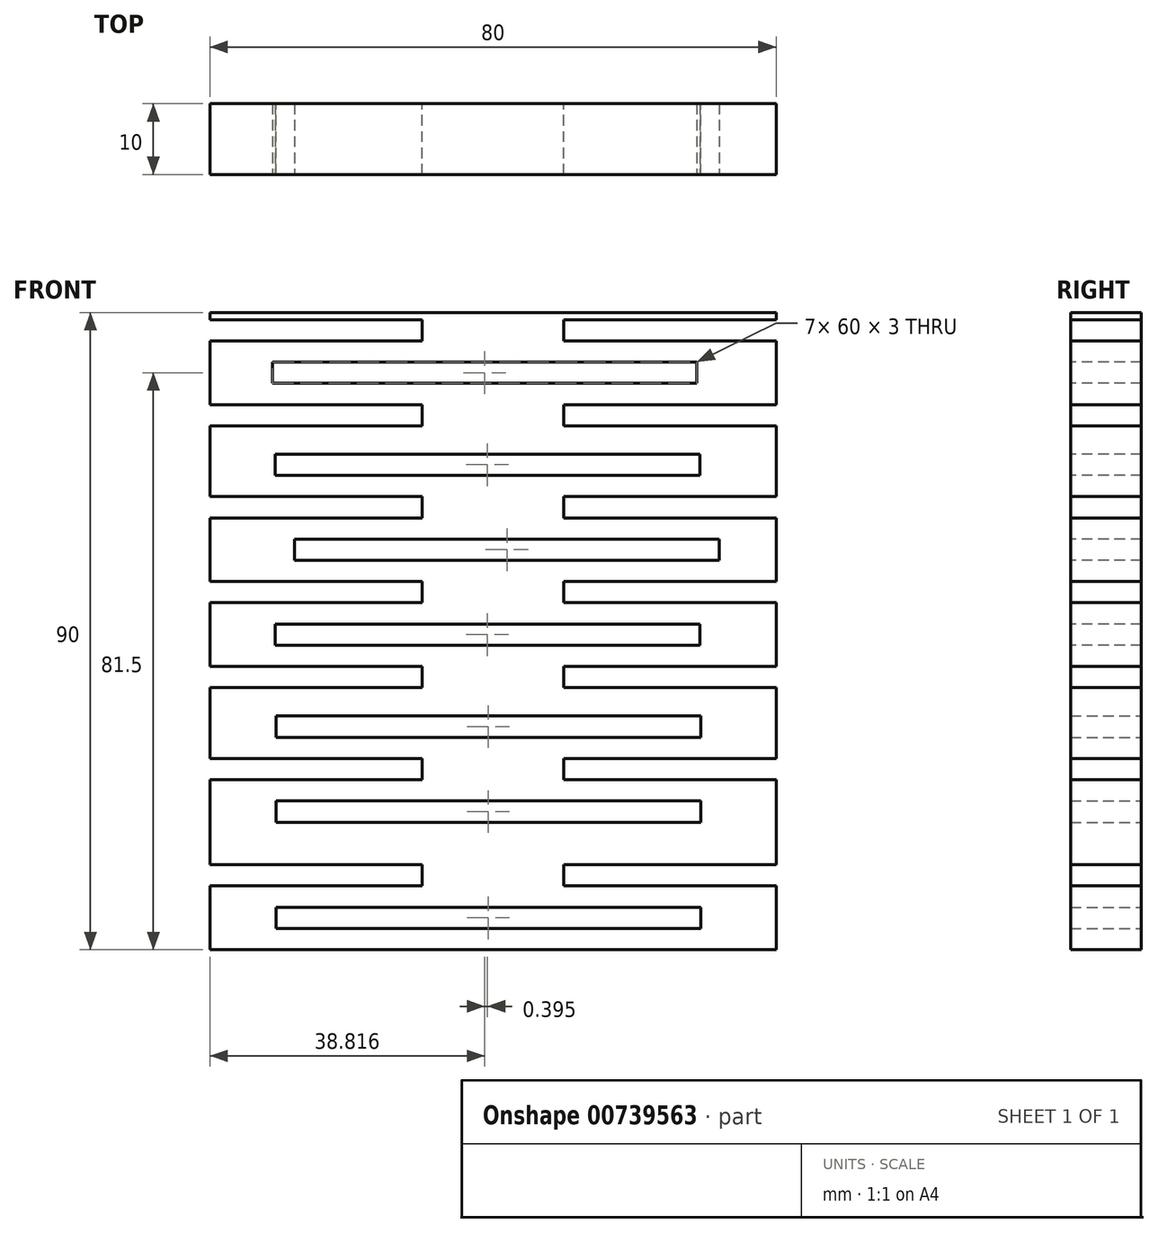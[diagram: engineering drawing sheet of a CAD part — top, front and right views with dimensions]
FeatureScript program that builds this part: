
annotation { "Feature Type Name" : "Feature", "Feature Type Description" : "" }
export const myFeature = defineFeature(function(context is Context, id is Id, definition is map)
    precondition{}
    {
        {
            var Q0;
            Q0=qCreatedBy(makeId("Front.planeOp"),FACE);
            var sketch = newSketch(context, id + "F0", { "sketchPlane" : qUnion([Q0])});
            skPoint(sketch, "E0.firstSnap0", {"position": v(1.21, 52.73) * mm});
            skPoint(sketch, "E0.left.start.orphan", {"position": v(1.21, 53.6) * mm});
            skPoint(sketch, "E1.top.end.orphan", {"position": v(-2.83, 53.6) * mm});
            skPoint(sketch, "E2.left.start.orphan", {"position": v(-45.92, 52.73) * mm});
            skPoint(sketch, "E2.right.start.orphan", {"position": v(48.35, 52.73) * mm});
            skLineSegment(sketch, "E3", {"start": v(40, -40) * mm, "end": v(40, 50) * mm});
            skLineSegment(sketch, "E4", {"start": v(-40, -40) * mm, "end": v(-40, 50) * mm});
            skLineSegment(sketch, "E5", {"start": v(40, 50) * mm, "end": v(-40, 50) * mm});
            skLineSegment(sketch, "E6", {"start": v(40, -40) * mm, "end": v(-40, -40) * mm});
            skPoint(sketch, "E7.start.orphan", {"position": v(-10, -31) * mm});
            skPoint(sketch, "E8.start.orphan", {"position": v(-0.3, -31) * mm});
            skPoint(sketch, "E9.end.orphan", {"position": v(-0.24, -22) * mm});
            skPoint(sketch, "E10.end.orphan", {"position": v(0, -10) * mm});
            skPoint(sketch, "E11.start.orphan", {"position": v(0, -7) * mm});
            skPoint(sketch, "E12.start.orphan", {"position": v(0, 0) * mm});
            skPoint(sketch, "E13.end.orphan", {"position": v(0, 12) * mm});
            skPoint(sketch, "E14.start.orphan", {"position": v(0, 24) * mm});
            skPoint(sketch, "E15.end.orphan", {"position": v(0, 36) * mm});
            skPoint(sketch, "E16.start.orphan", {"position": v(-40, 36) * mm});
            skPoint(sketch, "E17.start.orphan", {"position": v(40, 36) * mm});
            skPoint(sketch, "E18.start.orphan", {"position": v(0, 18) * mm});
            skPoint(sketch, "E19.start.orphan", {"position": v(40, 12) * mm});
            skPoint(sketch, "E20.start.orphan", {"position": v(40, 24) * mm});
            skPoint(sketch, "E21.start.orphan", {"position": v(-40, 24) * mm});
            skPoint(sketch, "E22.start.orphan", {"position": v(-40, 12) * mm});
            skPoint(sketch, "E23.start.orphan", {"position": v(-40, 0) * mm});
            skPoint(sketch, "E24.start.orphan", {"position": v(40, 0) * mm});
            skPoint(sketch, "E25.start.orphan", {"position": v(-0.24, -28) * mm});
            skLineSegment(sketch, "E26", {"start": v(0, 50) * mm, "end": v(0, -40) * mm});
            skLineSegment(sketch, "E27.bottom", {"start": v(-30.66, -37) * mm, "end": v(29.34, -37) * mm});
            skLineSegment(sketch, "E27.top", {"start": v(-30.66, -34) * mm, "end": v(29.34, -34) * mm});
            skLineSegment(sketch, "E27.left", {"start": v(-30.66, -37) * mm, "end": v(-30.66, -34) * mm});
            skLineSegment(sketch, "E27.right", {"start": v(29.34, -37) * mm, "end": v(29.34, -34) * mm});
            skLineSegment(sketch, "E28.bottom", {"start": v(-40, -28) * mm, "end": v(-10, -28) * mm});
            skLineSegment(sketch, "E28.top", {"start": v(-40, -31) * mm, "end": v(-10, -31) * mm});
            skLineSegment(sketch, "E28.left", {"start": v(-40, -28) * mm, "end": v(-40, -31) * mm});
            skLineSegment(sketch, "E28.right", {"start": v(-10, -28) * mm, "end": v(-10, -31) * mm});
            skLineSegment(sketch, "E29.bottom", {"start": v(40, -28) * mm, "end": v(10, -28) * mm});
            skLineSegment(sketch, "E29.top", {"start": v(40, -31) * mm, "end": v(10, -31) * mm});
            skLineSegment(sketch, "E29.left", {"start": v(40, -28) * mm, "end": v(40, -31) * mm});
            skLineSegment(sketch, "E29.right", {"start": v(10, -28) * mm, "end": v(10, -31) * mm});
            skLineSegment(sketch, "E30.bottom", {"start": v(-30.66, -19) * mm, "end": v(29.34, -19) * mm});
            skLineSegment(sketch, "E30.top", {"start": v(-30.66, -22) * mm, "end": v(29.34, -22) * mm});
            skLineSegment(sketch, "E30.left", {"start": v(-30.66, -19) * mm, "end": v(-30.66, -22) * mm});
            skLineSegment(sketch, "E30.right", {"start": v(29.34, -19) * mm, "end": v(29.34, -22) * mm});
            skLineSegment(sketch, "E31.bottom", {"start": v(-40, -13) * mm, "end": v(-10, -13) * mm});
            skLineSegment(sketch, "E31.top", {"start": v(-40, -16) * mm, "end": v(-10, -16) * mm});
            skLineSegment(sketch, "E31.left", {"start": v(-40, -13) * mm, "end": v(-40, -16) * mm});
            skLineSegment(sketch, "E31.right", {"start": v(-10, -13) * mm, "end": v(-10, -16) * mm});
            skLineSegment(sketch, "E32.bottom", {"start": v(10, -13) * mm, "end": v(40, -13) * mm});
            skLineSegment(sketch, "E32.top", {"start": v(10, -16) * mm, "end": v(40, -16) * mm});
            skLineSegment(sketch, "E32.left", {"start": v(10, -13) * mm, "end": v(10, -16) * mm});
            skLineSegment(sketch, "E32.right", {"start": v(40, -13) * mm, "end": v(40, -16) * mm});
            skLineSegment(sketch, "E33.bottom", {"start": v(-20.5, -16) * mm, "end": v(-21.1, -16) * mm});
            skLineSegment(sketch, "E33.top", {"start": v(-20.5, -19) * mm, "end": v(-21.1, -19) * mm});
            skLineSegment(sketch, "E34.bottom", {"start": v(-30.66, -7) * mm, "end": v(29.34, -7) * mm});
            skLineSegment(sketch, "E34.top", {"start": v(-30.66, -10) * mm, "end": v(29.34, -10) * mm});
            skLineSegment(sketch, "E34.left", {"start": v(-30.66, -7) * mm, "end": v(-30.66, -10) * mm});
            skLineSegment(sketch, "E34.right", {"start": v(29.34, -7) * mm, "end": v(29.34, -10) * mm});
            skSolve(sketch);
        }
        {
            var Q0;
            {var subQ9=sQuery(id+"F0.wireOp",EDGE,"E27.left");Q0=makeQuery(id+"F0.imprint","IMPRINT",FACE,{"disambiguationData":[TD([[makeQuery(id+"F0.imprint","IMPRINT",EDGE,{"derivedFrom":subQ9}),1.0]])]});}
            var Q1;
            {var subQ7=sQuery(id+"F0.wireOp",EDGE,"E27.right");Q1=makeQuery(id+"F0.imprint","IMPRINT",FACE,{"disambiguationData":[TD([[makeQuery(id+"F0.imprint","IMPRINT",EDGE,{"derivedFrom":subQ7}),-1.0]])]});}
            extrude(context, id + "F1", {"entities" : qUnion([Q0, Q1]), "depth" : 10 * mm, "offsetDistance" : 25 * mm});
        }
        {
            var Q0;
            Q0=makeQuery(id+"F1.opExtrude","CAP_FACE",FACE,{"disambiguationData":[OSD([sQuery(id+"F0.wireOp",EDGE,"E3"),sQuery(id+"F0.wireOp",EDGE,"E4"),sQuery(id+"F0.wireOp",EDGE,"E5"),sQuery(id+"F0.wireOp",EDGE,"E6"),sQuery(id+"F0.wireOp",EDGE,"E27.bottom"),sQuery(id+"F0.wireOp",EDGE,"E27.top"),sQuery(id+"F0.wireOp",EDGE,"E27.left"),sQuery(id+"F0.wireOp",EDGE,"E27.right"),sQuery(id+"F0.wireOp",EDGE,"E28.bottom"),sQuery(id+"F0.wireOp",EDGE,"E28.top"),sQuery(id+"F0.wireOp",EDGE,"E28.right"),sQuery(id+"F0.wireOp",EDGE,"E29.bottom"),sQuery(id+"F0.wireOp",EDGE,"E29.top"),sQuery(id+"F0.wireOp",EDGE,"E29.right"),sQuery(id+"F0.wireOp",EDGE,"E30.bottom"),sQuery(id+"F0.wireOp",EDGE,"E30.top"),sQuery(id+"F0.wireOp",EDGE,"E30.left"),sQuery(id+"F0.wireOp",EDGE,"E30.right"),sQuery(id+"F0.wireOp",EDGE,"E31.bottom"),sQuery(id+"F0.wireOp",EDGE,"E31.top"),sQuery(id+"F0.wireOp",EDGE,"E31.right"),sQuery(id+"F0.wireOp",EDGE,"E32.bottom"),sQuery(id+"F0.wireOp",EDGE,"E32.top"),sQuery(id+"F0.wireOp",EDGE,"E32.left"),sQuery(id+"F0.wireOp",EDGE,"E33.bottom"),sQuery(id+"F0.wireOp",EDGE,"E33.top"),sQuery(id+"F0.wireOp",EDGE,"E34.bottom"),sQuery(id+"F0.wireOp",EDGE,"E34.top"),sQuery(id+"F0.wireOp",EDGE,"E34.left"),sQuery(id+"F0.wireOp",EDGE,"E34.right")])],"isStart":false});
            var sketch = newSketch(context, id + "F2", { "sketchPlane" : qUnion([Q0])});
            skLineSegment(sketch, "E35.bottom", {"start": v(-40, 0) * mm, "end": v(-10, 0) * mm});
            skLineSegment(sketch, "E35.top", {"start": v(-40, -3) * mm, "end": v(-10, -3) * mm});
            skLineSegment(sketch, "E35.left", {"start": v(-40, 0) * mm, "end": v(-40, -3) * mm});
            skLineSegment(sketch, "E35.right", {"start": v(-10, 0) * mm, "end": v(-10, -3) * mm});
            skLineSegment(sketch, "E36.bottom", {"start": v(40, 0) * mm, "end": v(10, 0) * mm});
            skLineSegment(sketch, "E36.top", {"start": v(40, -3) * mm, "end": v(10, -3) * mm});
            skLineSegment(sketch, "E36.left", {"start": v(40, 0) * mm, "end": v(40, -3) * mm});
            skLineSegment(sketch, "E36.right", {"start": v(10, 0) * mm, "end": v(10, -3) * mm});
            skLineSegment(sketch, "E37.bottom", {"start": v(-30.79, 6) * mm, "end": v(29.21, 6) * mm});
            skLineSegment(sketch, "E37.top", {"start": v(-30.79, 3) * mm, "end": v(29.21, 3) * mm});
            skLineSegment(sketch, "E37.left", {"start": v(-30.79, 6) * mm, "end": v(-30.79, 3) * mm});
            skLineSegment(sketch, "E37.right", {"start": v(29.21, 6) * mm, "end": v(29.21, 3) * mm});
            skLineSegment(sketch, "E38.bottom", {"start": v(-40, 12) * mm, "end": v(-10, 12) * mm});
            skLineSegment(sketch, "E38.top", {"start": v(-40, 9) * mm, "end": v(-10, 9) * mm});
            skLineSegment(sketch, "E38.left", {"start": v(-40, 12) * mm, "end": v(-40, 9) * mm});
            skLineSegment(sketch, "E38.right", {"start": v(-10, 12) * mm, "end": v(-10, 9) * mm});
            skLineSegment(sketch, "E39.bottom", {"start": v(10, 12) * mm, "end": v(40, 12) * mm});
            skLineSegment(sketch, "E39.top", {"start": v(10, 9) * mm, "end": v(40, 9) * mm});
            skLineSegment(sketch, "E39.left", {"start": v(10, 12) * mm, "end": v(10, 9) * mm});
            skLineSegment(sketch, "E39.right", {"start": v(40, 12) * mm, "end": v(40, 9) * mm});
            skLineSegment(sketch, "E40.bottom", {"start": v(-28.03, 18) * mm, "end": v(31.97, 18) * mm});
            skLineSegment(sketch, "E40.top", {"start": v(-28.03, 15) * mm, "end": v(31.97, 15) * mm});
            skLineSegment(sketch, "E40.left", {"start": v(-28.03, 18) * mm, "end": v(-28.03, 15) * mm});
            skLineSegment(sketch, "E40.right", {"start": v(31.97, 18) * mm, "end": v(31.97, 15) * mm});
            skLineSegment(sketch, "E41.bottom", {"start": v(-40, 21) * mm, "end": v(-10, 21) * mm});
            skLineSegment(sketch, "E41.top", {"start": v(-40, 24) * mm, "end": v(-10, 24) * mm});
            skLineSegment(sketch, "E41.left", {"start": v(-40, 21) * mm, "end": v(-40, 24) * mm});
            skLineSegment(sketch, "E41.right", {"start": v(-10, 21) * mm, "end": v(-10, 24) * mm});
            skLineSegment(sketch, "E42.bottom", {"start": v(40, 24) * mm, "end": v(10, 24) * mm});
            skLineSegment(sketch, "E42.top", {"start": v(40, 21) * mm, "end": v(10, 21) * mm});
            skLineSegment(sketch, "E42.left", {"start": v(40, 24) * mm, "end": v(40, 21) * mm});
            skLineSegment(sketch, "E42.right", {"start": v(10, 24) * mm, "end": v(10, 21) * mm});
            skLineSegment(sketch, "E43.bottom", {"start": v(-30.79, 30) * mm, "end": v(29.21, 30) * mm});
            skLineSegment(sketch, "E43.top", {"start": v(-30.79, 27) * mm, "end": v(29.21, 27) * mm});
            skLineSegment(sketch, "E43.left", {"start": v(-30.79, 30) * mm, "end": v(-30.79, 27) * mm});
            skLineSegment(sketch, "E43.right", {"start": v(29.21, 30) * mm, "end": v(29.21, 27) * mm});
            skSolve(sketch);
        }
        {
            var Q0;
            Q0 = qSketchRegion(id + "F2", true);
            extrude(context, id + "F3", {"entities" : qUnion([Q0]), "operationType" : NewBodyOperationType.REMOVE, "oppositeDirection" : true, "depth" : 25 * mm, "offsetDistance" : 25 * mm});
        }
        {
            var Q0;
            Q0=makeQuery(id+"F1.opExtrude","CAP_FACE",FACE,{"disambiguationData":[OSD([sQuery(id+"F0.wireOp",EDGE,"E3"),sQuery(id+"F0.wireOp",EDGE,"E4"),sQuery(id+"F0.wireOp",EDGE,"E5"),sQuery(id+"F0.wireOp",EDGE,"E6"),sQuery(id+"F0.wireOp",EDGE,"E27.bottom"),sQuery(id+"F0.wireOp",EDGE,"E27.top"),sQuery(id+"F0.wireOp",EDGE,"E27.left"),sQuery(id+"F0.wireOp",EDGE,"E27.right"),sQuery(id+"F0.wireOp",EDGE,"E28.bottom"),sQuery(id+"F0.wireOp",EDGE,"E28.top"),sQuery(id+"F0.wireOp",EDGE,"E28.right"),sQuery(id+"F0.wireOp",EDGE,"E29.bottom"),sQuery(id+"F0.wireOp",EDGE,"E29.top"),sQuery(id+"F0.wireOp",EDGE,"E29.right"),sQuery(id+"F0.wireOp",EDGE,"E30.bottom"),sQuery(id+"F0.wireOp",EDGE,"E30.top"),sQuery(id+"F0.wireOp",EDGE,"E30.left"),sQuery(id+"F0.wireOp",EDGE,"E30.right"),sQuery(id+"F0.wireOp",EDGE,"E31.bottom"),sQuery(id+"F0.wireOp",EDGE,"E31.top"),sQuery(id+"F0.wireOp",EDGE,"E31.right"),sQuery(id+"F0.wireOp",EDGE,"E32.bottom"),sQuery(id+"F0.wireOp",EDGE,"E32.top"),sQuery(id+"F0.wireOp",EDGE,"E32.left"),sQuery(id+"F0.wireOp",EDGE,"E33.bottom"),sQuery(id+"F0.wireOp",EDGE,"E33.top"),sQuery(id+"F0.wireOp",EDGE,"E34.bottom"),sQuery(id+"F0.wireOp",EDGE,"E34.top"),sQuery(id+"F0.wireOp",EDGE,"E34.left"),sQuery(id+"F0.wireOp",EDGE,"E34.right")])],"isStart":false});
            var sketch = newSketch(context, id + "F4", { "sketchPlane" : qUnion([Q0])});
            skLineSegment(sketch, "E44.bottom", {"start": v(-40, 37) * mm, "end": v(-10, 37) * mm});
            skLineSegment(sketch, "E44.top", {"start": v(-40, 34) * mm, "end": v(-10, 34) * mm});
            skLineSegment(sketch, "E44.left", {"start": v(-40, 37) * mm, "end": v(-40, 34) * mm});
            skLineSegment(sketch, "E44.right", {"start": v(-10, 37) * mm, "end": v(-10, 34) * mm});
            skLineSegment(sketch, "E45.bottom", {"start": v(40, 37) * mm, "end": v(10, 37) * mm});
            skLineSegment(sketch, "E45.top", {"start": v(40, 34) * mm, "end": v(10, 34) * mm});
            skLineSegment(sketch, "E45.left", {"start": v(40, 37) * mm, "end": v(40, 34) * mm});
            skLineSegment(sketch, "E45.right", {"start": v(10, 37) * mm, "end": v(10, 34) * mm});
            skLineSegment(sketch, "E46.bottom", {"start": v(-31.18, 43) * mm, "end": v(28.82, 43) * mm});
            skLineSegment(sketch, "E46.top", {"start": v(-31.18, 40) * mm, "end": v(28.82, 40) * mm});
            skLineSegment(sketch, "E46.left", {"start": v(-31.18, 43) * mm, "end": v(-31.18, 40) * mm});
            skLineSegment(sketch, "E46.right", {"start": v(28.82, 43) * mm, "end": v(28.82, 40) * mm});
            skLineSegment(sketch, "E47.bottom", {"start": v(-40, 49) * mm, "end": v(-10, 49) * mm});
            skLineSegment(sketch, "E47.top", {"start": v(-40, 46) * mm, "end": v(-10, 46) * mm});
            skLineSegment(sketch, "E47.left", {"start": v(-40, 49) * mm, "end": v(-40, 46) * mm});
            skLineSegment(sketch, "E47.right", {"start": v(-10, 49) * mm, "end": v(-10, 46) * mm});
            skLineSegment(sketch, "E48.bottom", {"start": v(10, 49) * mm, "end": v(40, 49) * mm});
            skLineSegment(sketch, "E48.top", {"start": v(10, 46) * mm, "end": v(40, 46) * mm});
            skLineSegment(sketch, "E48.left", {"start": v(10, 49) * mm, "end": v(10, 46) * mm});
            skLineSegment(sketch, "E48.right", {"start": v(40, 49) * mm, "end": v(40, 46) * mm});
            skSolve(sketch);
        }
        {
            var Q0;
            Q0 = qSketchRegion(id + "F4", true);
            extrude(context, id + "F5", {"entities" : qUnion([Q0]), "operationType" : NewBodyOperationType.REMOVE, "oppositeDirection" : true, "depth" : 25 * mm, "offsetDistance" : 25 * mm});
        }
    });
